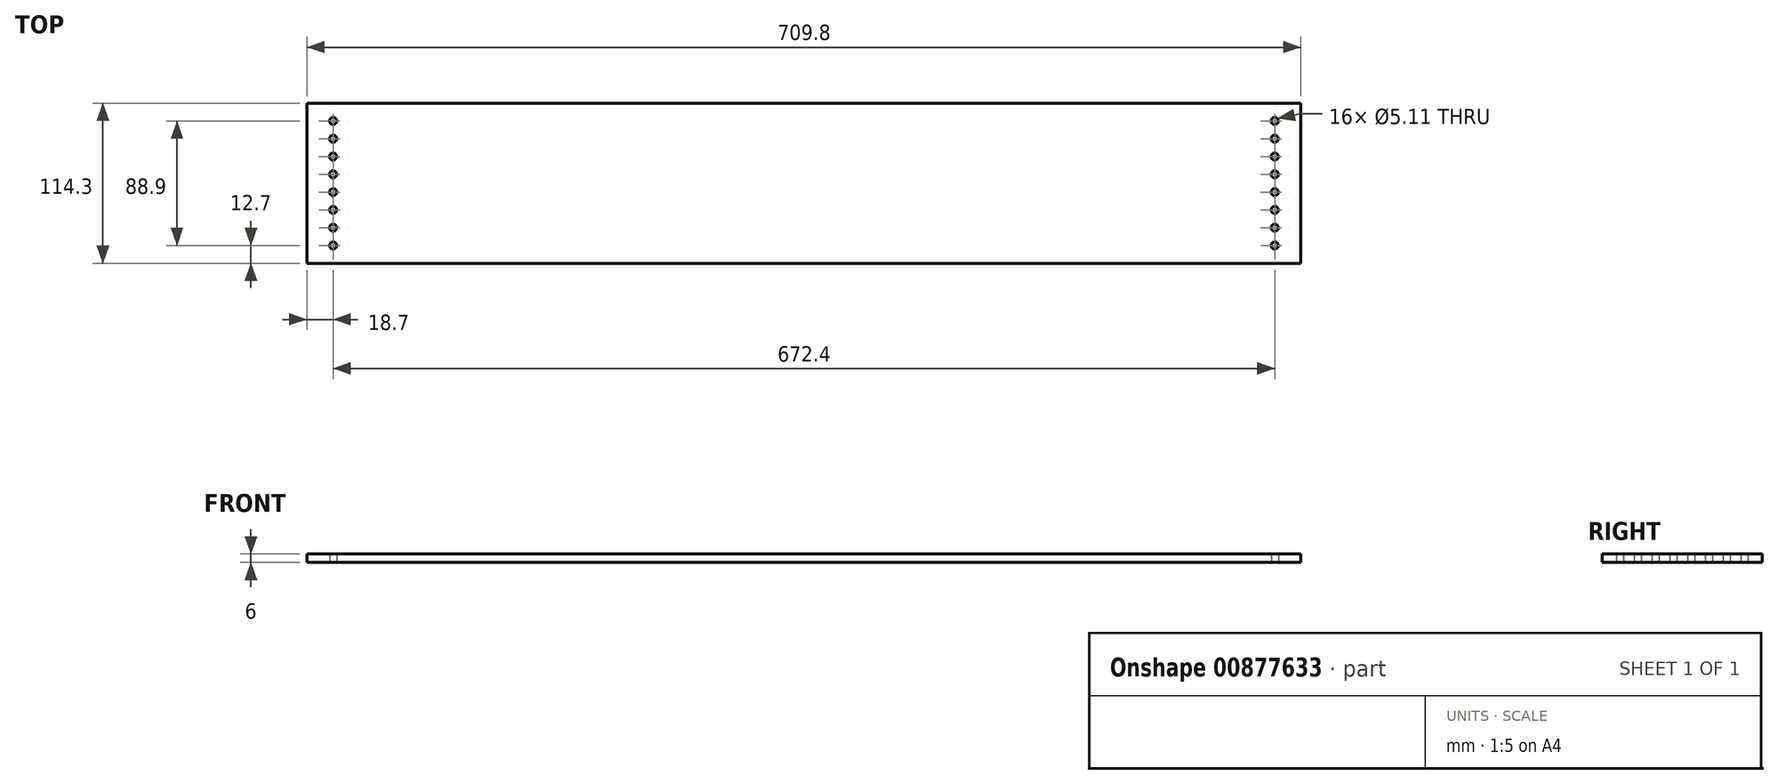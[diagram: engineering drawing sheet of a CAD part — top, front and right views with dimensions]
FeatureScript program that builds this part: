
annotation { "Feature Type Name" : "Feature", "Feature Type Description" : "" }
export const myFeature = defineFeature(function(context is Context, id is Id, definition is map)
    precondition{}
    {
        {
            var Q0;
            Q0=qCreatedBy(makeId("Top.planeOp"),FACE);
            var sketch = newSketch(context, id + "F0", { "sketchPlane" : qUnion([Q0])});
            skLineSegment(sketch, "E0.bottom", {"start": v(-354.9, 57.15) * mm, "end": v(354.9, 57.15) * mm});
            skLineSegment(sketch, "E0.top", {"start": v(-354.9, -57.15) * mm, "end": v(354.9, -57.15) * mm});
            skLineSegment(sketch, "E0.left", {"start": v(-354.9, 57.15) * mm, "end": v(-354.9, -57.15) * mm});
            skLineSegment(sketch, "E0.right", {"start": v(354.9, 57.15) * mm, "end": v(354.9, -57.15) * mm});
            skPoint(sketch, "E0.middle", {"position": v(0, 0) * mm});
            skCircle(sketch, "E1", {"center": v(-336.2, 44.45) * mm, "radius": 2.55 * mm});
            skCircle(sketch, "E2.0.1.0", {"center": v(-336.2, 31.75) * mm, "radius": 2.55 * mm});
            skCircle(sketch, "E2.0.2.0", {"center": v(-336.2, 19.05) * mm, "radius": 2.55 * mm});
            skCircle(sketch, "E2.0.3.0", {"center": v(-336.2, 6.35) * mm, "radius": 2.55 * mm});
            skCircle(sketch, "E2.0.4.0", {"center": v(-336.2, -6.35) * mm, "radius": 2.55 * mm});
            skCircle(sketch, "E2.0.5.0", {"center": v(-336.2, -19.05) * mm, "radius": 2.55 * mm});
            skLineSegment(sketch, "E2.direction1", {"start": v(-336.2, 44.45) * mm, "end": v(-285.4, 44.45) * mm, "construction": true});
            skLineSegment(sketch, "E2.direction2", {"start": v(-336.2, 44.45) * mm, "end": v(-336.2, 31.75) * mm, "construction": true});
            skCircle(sketch, "E3", {"center": v(336.2, 44.45) * mm, "radius": 2.55 * mm});
            skCircle(sketch, "E4.0.1.0", {"center": v(336.2, 31.75) * mm, "radius": 2.55 * mm});
            skCircle(sketch, "E4.0.2.0", {"center": v(336.2, 19.05) * mm, "radius": 2.55 * mm});
            skCircle(sketch, "E4.0.3.0", {"center": v(336.2, 6.35) * mm, "radius": 2.55 * mm});
            skCircle(sketch, "E4.0.4.0", {"center": v(336.2, -6.35) * mm, "radius": 2.55 * mm});
            skCircle(sketch, "E4.0.5.0", {"center": v(336.2, -19.05) * mm, "radius": 2.55 * mm});
            skCircle(sketch, "E4.0.6.0", {"center": v(336.2, -31.75) * mm, "radius": 2.55 * mm});
            skCircle(sketch, "E4.0.7.0", {"center": v(336.2, -44.45) * mm, "radius": 2.55 * mm});
            skLineSegment(sketch, "E4.direction1", {"start": v(336.2, 44.45) * mm, "end": v(336.2, 44.45) * mm});
            skLineSegment(sketch, "E4.direction2", {"start": v(336.2, 44.45) * mm, "end": v(336.2, 31.75) * mm, "construction": true});
            skCircle(sketch, "E5.0.0.6", {"center": v(-336.2, -31.75) * mm, "radius": 2.55 * mm});
            skCircle(sketch, "E5.0.0.7", {"center": v(-336.2, -44.45) * mm, "radius": 2.55 * mm});
            skSolve(sketch);
        }
        {
            var Q0;
            Q0=makeQuery(id+"F0.imprint","IMPRINT",FACE,{"disambiguationData":[TD([[makeQuery(id+"F0.imprint","IMPRINT",EDGE,{"derivedFrom":sQuery(id+"F0.wireOp",EDGE,"E0.bottom")}),-1.0]])]});
            extrude(context, id + "F1", {"entities" : qUnion([Q0]), "depth" : 6 * mm, "offsetDistance" : 25.4 * mm});
        }
    });
